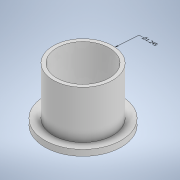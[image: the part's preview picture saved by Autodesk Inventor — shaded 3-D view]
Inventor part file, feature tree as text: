
AUTODESK INVENTOR PART (.ipt)
format: ipt  version: 2021.2 (Build 252289000, 289)  size: 386,560 bytes
history: native  units: in
note: dims shown in document units (in); Inventor stores cm internally (conversion verified against a paired STEP export)
features: extrude x4, sketch x4, other x2
ambient origin geometry x8: Origin, YZ Plane, XZ Plane, XY Plane, X Axis, Y Axis, Z Axis, Center Point
bodies: Solid1 (feature_tree)
feature tree (10):
  other  "Annotations"
  extrude  "Extrusion1"  Depth=0.125in TaperAngle=0.0deg
  extrude  "Extrusion3"  Depth=1.095in
  extrude  "Extrusion4"  TaperAngle=0.0deg  [1 undecoded]
  extrude  "Extrusion5"  Depth=0.05in TaperAngle=0.0deg
  sketch  "Sketch1"  dims[d0=1.6in d1=0.125in d2=0.0in]
  sketch  "Sketch2"  dims[d3=1.245in d4=1.095in]
  sketch  "Sketch3"  dims[d7=1.0in d8=0.0in]
  sketch  "Sketch4"  dims[d11=0.025in d12=0.0in d17=0.05in d18=0.0in d15=1.8251in d16=1.245in]
  other  "Diameter Dimension 1"
note: 1 required parameter value undecoded (feature->parameter linkage not recoverable at this tier; creation-order binding heuristic only, values carry confidence <= 0.55)
